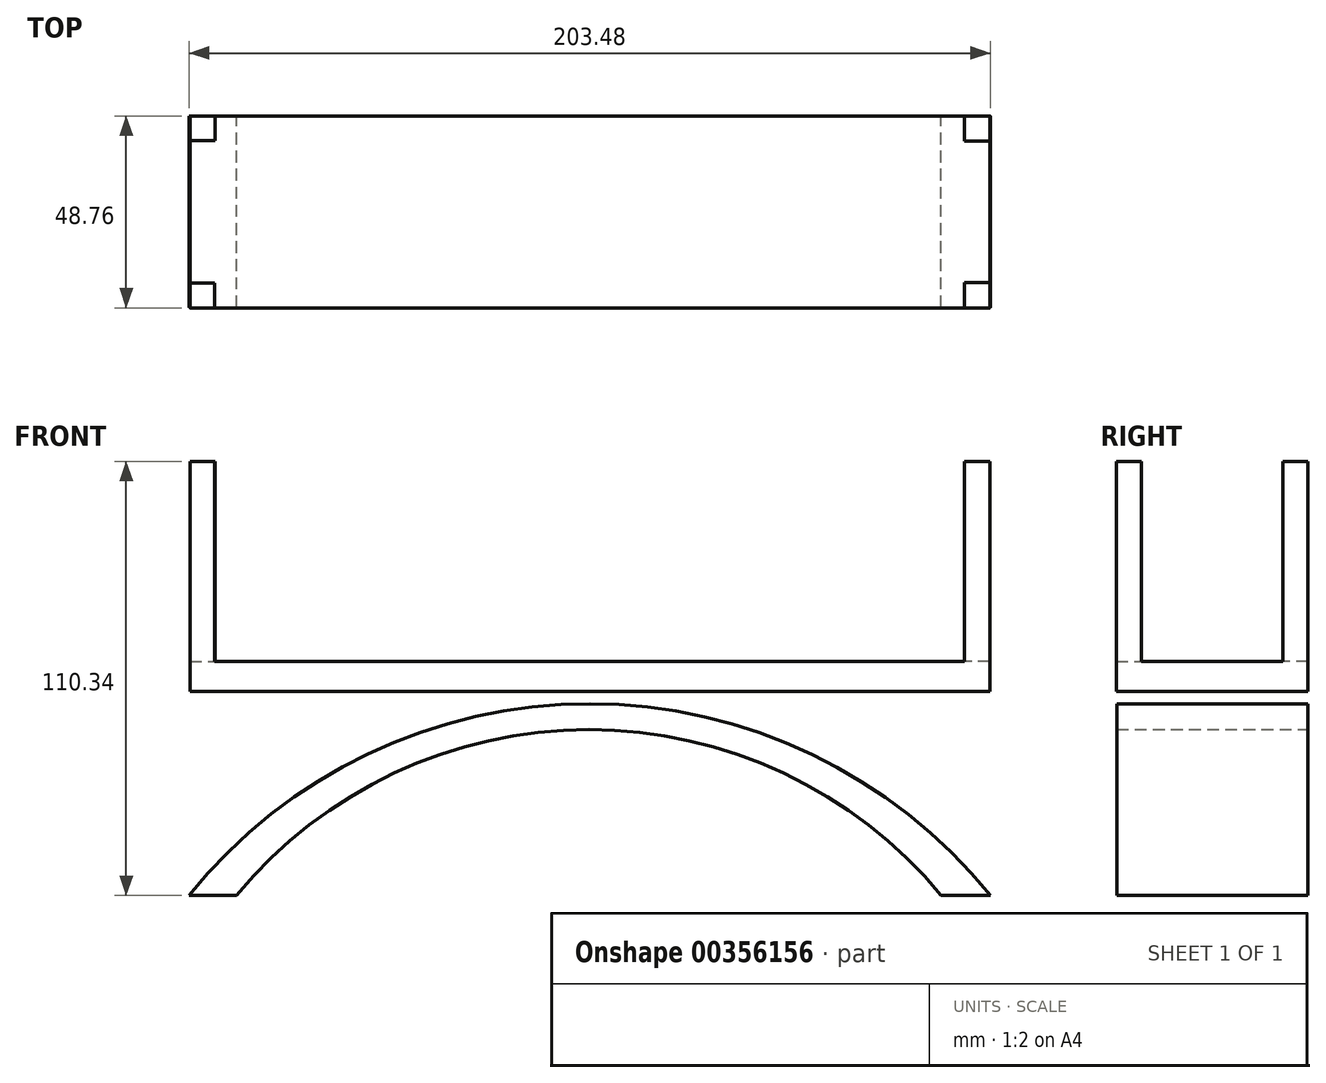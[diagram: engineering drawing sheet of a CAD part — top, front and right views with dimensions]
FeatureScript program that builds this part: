
annotation { "Feature Type Name" : "Feature", "Feature Type Description" : "" }
export const myFeature = defineFeature(function(context is Context, id is Id, definition is map)
    precondition{}
    {
        {
            var Q0;
            Q0=qCreatedBy(makeId("Front.planeOp"),FACE);
            var sketch = newSketch(context, id + "F0", { "sketchPlane" : qUnion([Q0])});
            skLineSegment(sketch, "E0.bottom", {"start": v(101.6, 3.81) * mm, "end": v(-101.6, 3.81) * mm});
            skLineSegment(sketch, "E0.top", {"start": v(101.6, -3.81) * mm, "end": v(-101.6, -3.81) * mm});
            skLineSegment(sketch, "E0.left", {"start": v(101.6, 3.81) * mm, "end": v(101.6, -3.81) * mm});
            skLineSegment(sketch, "E0.right", {"start": v(-101.6, 3.81) * mm, "end": v(-101.6, -3.81) * mm});
            skPoint(sketch, "E0.middle", {"position": v(0, 0) * mm});
            skSolve(sketch);
        }
        {
            var Q0;
            Q0=makeQuery(id+"F0.imprint","IMPRINT",FACE,{"disambiguationData":[TD([[makeQuery(id+"F0.imprint","IMPRINT",EDGE,{"derivedFrom":sQuery(id+"F0.wireOp",EDGE,"E0.bottom")}),1.0]])]});
            extrude(context, id + "F1", {"entities" : qUnion([Q0]), "depth" : 48.76 * mm});
        }
        {
            var Q0;
            Q0=makeQuery(id+"F1.opExtrude","SWEPT_FACE",FACE,{"disambiguationData":[OSD([sQuery(id+"F0.wireOp",EDGE,"E0.bottom")])]});
            var sketch = newSketch(context, id + "F2", { "sketchPlane" : qUnion([Q0])});
            skLineSegment(sketch, "E1.bottom", {"start": v(-101.6, 0) * mm, "end": v(-95.17, 0) * mm});
            skLineSegment(sketch, "E1.top", {"start": v(-101.6, -6.24) * mm, "end": v(-95.17, -6.24) * mm});
            skLineSegment(sketch, "E1.left", {"start": v(-101.6, 0) * mm, "end": v(-101.6, -6.24) * mm});
            skLineSegment(sketch, "E1.right", {"start": v(-95.17, 0) * mm, "end": v(-95.17, -6.24) * mm});
            skLineSegment(sketch, "E2.bottom", {"start": v(-101.6, -48.76) * mm, "end": v(-95.38, -48.76) * mm});
            skLineSegment(sketch, "E2.top", {"start": v(-101.6, -42.52) * mm, "end": v(-95.38, -42.52) * mm});
            skLineSegment(sketch, "E2.left", {"start": v(-101.6, -48.76) * mm, "end": v(-101.6, -42.52) * mm});
            skLineSegment(sketch, "E2.right", {"start": v(-95.38, -48.76) * mm, "end": v(-95.38, -42.52) * mm});
            skLineSegment(sketch, "E3.bottom", {"start": v(101.6, 0) * mm, "end": v(95.13, 0) * mm});
            skLineSegment(sketch, "E3.top", {"start": v(101.6, -6.44) * mm, "end": v(95.13, -6.44) * mm});
            skLineSegment(sketch, "E3.left", {"start": v(101.6, 0) * mm, "end": v(101.6, -6.44) * mm});
            skLineSegment(sketch, "E3.right", {"start": v(95.13, 0) * mm, "end": v(95.13, -6.44) * mm});
            skLineSegment(sketch, "E4.bottom", {"start": v(101.6, -48.76) * mm, "end": v(95.13, -48.76) * mm});
            skLineSegment(sketch, "E4.top", {"start": v(101.6, -42.32) * mm, "end": v(95.13, -42.32) * mm});
            skLineSegment(sketch, "E4.left", {"start": v(101.6, -48.76) * mm, "end": v(101.6, -42.32) * mm});
            skLineSegment(sketch, "E4.right", {"start": v(95.13, -48.76) * mm, "end": v(95.13, -42.32) * mm});
            skSolve(sketch);
        }
        {
            var Q0;
            Q0=qSketchRegion(id+"F2",true);
            extrude(context, id + "F3", {"entities" : qUnion([Q0]), "operationType" : NewBodyOperationType.ADD, "depth" : 50.8 * mm});
        }
        {
            var Q0;
            Q0=qCreatedBy(makeId("Front.planeOp"),FACE);
            var sketch = newSketch(context, id + "F4", { "sketchPlane" : qUnion([Q0])});
            skArc(sketch, "E5", {"start": v(101.7, -55.73) * mm, "mid": v(0, -7) * mm, "end": v(-101.77, -55.61) * mm});
            skLineSegment(sketch, "E6", {"start": v(-101.77, -55.61) * mm, "end": v(-89.74, -55.61) * mm});
            skLineSegment(sketch, "E7", {"start": v(89.22, -55.61) * mm, "end": v(101.7, -55.73) * mm});
            skArc(sketch, "E8", {"start": v(89.22, -55.61) * mm, "mid": v(-0.26, -13.56) * mm, "end": v(-89.74, -55.61) * mm});
            skSolve(sketch);
        }
        {
            var Q0;
            Q0=makeQuery(id+"F4.imprint","IMPRINT",FACE,{"disambiguationData":[TD([[makeQuery(id+"F4.imprint","IMPRINT",EDGE,{"derivedFrom":sQuery(id+"F4.wireOp",EDGE,"E5")}),1.0]])]});
            extrude(context, id + "F5", {"entities" : qUnion([Q0]), "operationType" : NewBodyOperationType.ADD, "depth" : 48.64 * mm});
        }
        {
            var Q0;
            Q0=qCreatedBy(makeId("Front.planeOp"),FACE);
            var sketch = newSketch(context, id + "F6", { "sketchPlane" : qUnion([Q0])});
            skLineSegment(sketch, "E9", {"start": v(-101.33, -3.82) * mm, "end": v(-101.33, -55.17) * mm});
            skSolve(sketch);
        }
        {
            var Q0;
            Q0=qSketchRegion(id+"F6",true);
            var Q1;
            Q1=sQuery(id+"F6.wireOp",EDGE,"E9");
            extrude(context, id + "F7", {"entities" : qUnion([Q0]), "bodyType" : ToolBodyType.SURFACE, "operationType" : NewBodyOperationType.ADD, "surfaceEntities" : qUnion([Q1]), "depth" : 48.73 * mm});
        }
        {
            var Q0;
            Q0=qCreatedBy(makeId("Front.planeOp"),FACE);
            var sketch = newSketch(context, id + "F8", { "sketchPlane" : qUnion([Q0])});
            skLineSegment(sketch, "E10", {"start": v(101.72, -3.53) * mm, "end": v(101.72, -55.63) * mm});
            skSolve(sketch);
        }
        {
            var Q0;
            Q0=qSketchRegion(id+"F8",true);
            var Q1;
            Q1=sQuery(id+"F8.wireOp",EDGE,"E10");
            extrude(context, id + "F9", {"entities" : qUnion([Q0]), "bodyType" : ToolBodyType.SURFACE, "surfaceEntities" : qUnion([Q1]), "depth" : 48.07 * mm});
        }
        {
            var Q0;
            Q0=qCreatedBy(makeId("Front.planeOp"),FACE);
            var sketch = newSketch(context, id + "F10", { "sketchPlane" : qUnion([Q0])});
            skLineSegment(sketch, "E11", {"start": v(-88.16, -4.41) * mm, "end": v(-88.16, -40.95) * mm});
            skLineSegment(sketch, "E12", {"start": v(-73.73, -4.41) * mm, "end": v(-73.73, -30.55) * mm});
            skLineSegment(sketch, "E13", {"start": v(-59.3, -3.82) * mm, "end": v(-59.3, -20.82) * mm});
            skLineSegment(sketch, "E14", {"start": v(-45.54, -3.82) * mm, "end": v(-45.54, -16.45) * mm});
            skLineSegment(sketch, "E15", {"start": v(89.08, -3.86) * mm, "end": v(89.08, -42.03) * mm});
            skLineSegment(sketch, "E16", {"start": v(74.3, -3.96) * mm, "end": v(74.3, -30.26) * mm});
            skLineSegment(sketch, "E17", {"start": v(237.1, -5.3) * mm, "end": v(237.1, -37.65) * mm});
            skLineSegment(sketch, "E18", {"start": v(59.2, -3.72) * mm, "end": v(59.2, -21.49) * mm});
            skLineSegment(sketch, "E19", {"start": v(43.4, -3.97) * mm, "end": v(43.4, -14.77) * mm});
            skSolve(sketch);
        }
        {
            var Q0;
            Q0=sQuery(id+"F10.wireOp",EDGE,"E11");
            var Q1;
            Q1=sQuery(id+"F10.wireOp",EDGE,"E12");
            var Q2;
            Q2=sQuery(id+"F10.wireOp",EDGE,"E13");
            var Q3;
            Q3=sQuery(id+"F10.wireOp",EDGE,"E14");
            var Q4;
            Q4=sQuery(id+"F10.wireOp",EDGE,"E19");
            var Q5;
            Q5=sQuery(id+"F10.wireOp",EDGE,"E18");
            var Q6;
            Q6=sQuery(id+"F10.wireOp",EDGE,"E16");
            var Q7;
            Q7=sQuery(id+"F10.wireOp",EDGE,"E15");
            extrude(context, id + "F11", {"bodyType" : ToolBodyType.SURFACE, "surfaceEntities" : qUnion([Q0, Q1, Q2, Q3, Q4, Q5, Q6, Q7]), "depth" : 48.62 * mm});
        }
        {
            var Q0;
            Q0=makeQuery(id+"F1.opExtrude","SWEPT_FACE",FACE,{"disambiguationData":[OSD([sQuery(id+"F0.wireOp",EDGE,"E0.bottom")])]});
            var sketch = newSketch(context, id + "F12", { "sketchPlane" : qUnion([Q0])});
            skLineSegment(sketch, "E20", {"start": v(-101.6, -24.38) * mm, "end": v(101.6, -24.38) * mm});
            skSolve(sketch);
        }
        {
            var Q0;
            Q0=qSketchRegion(id+"F12",true);
            var Q1;
            Q1=sQuery(id+"F12.wireOp",EDGE,"E20");
            extrude(context, id + "F13", {"entities" : qUnion([Q0]), "bodyType" : ToolBodyType.SURFACE, "surfaceEntities" : qUnion([Q1]), "depth" : 1.84 * mm});
        }
    });
